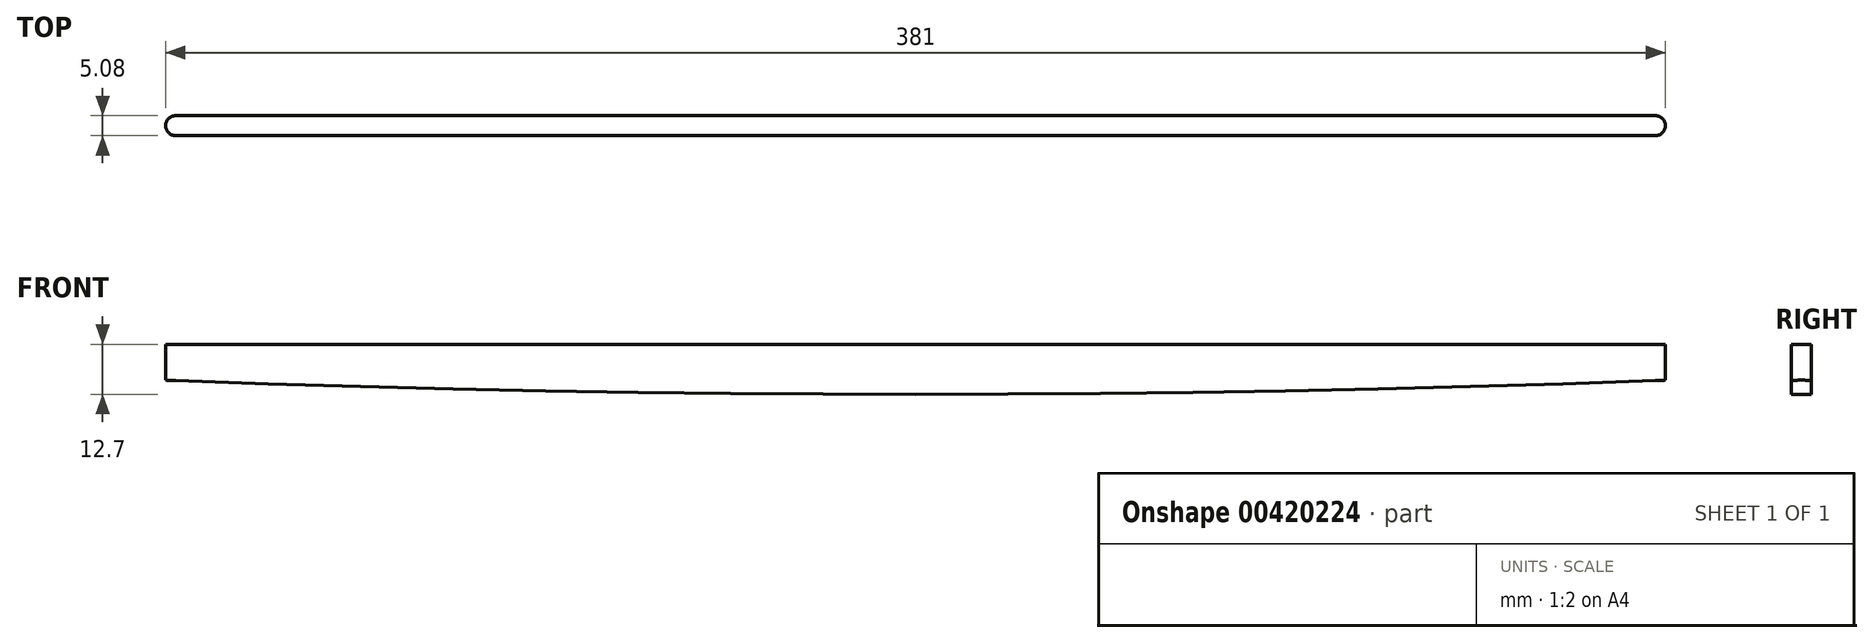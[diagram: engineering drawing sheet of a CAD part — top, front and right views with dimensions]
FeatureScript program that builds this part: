
annotation { "Feature Type Name" : "Feature", "Feature Type Description" : "" }
export const myFeature = defineFeature(function(context is Context, id is Id, definition is map)
    precondition{}
    {
        {
            var Q0;
            Q0=qCreatedBy(makeId("Front.planeOp"),FACE);
            var sketch = newSketch(context, id + "F0", { "sketchPlane" : qUnion([Q0])});
            skLineSegment(sketch, "E0", {"start": v(-319.44, 0) * mm, "end": v(61.56, 0) * mm});
            skArc(sketch, "E1", {"start": v(-319.44, -9.13) * mm, "mid": v(-128.94, -12.7) * mm, "end": v(61.56, -9.13) * mm});
            skPoint(sketch, "E2", {"position": v(-128.94, 0) * mm});
            skLineSegment(sketch, "E3", {"start": v(-128.94, 0) * mm, "end": v(-128.94, -12.7) * mm});
            skLineSegment(sketch, "E4", {"start": v(61.56, -9.13) * mm, "end": v(61.56, 0) * mm});
            skLineSegment(sketch, "E5", {"start": v(-319.44, 0) * mm, "end": v(-319.44, -9.13) * mm});
            skSolve(sketch);
        }
        {
            var Q0;
            Q0 = qSketchRegion(id + "F0", true);
            extrude(context, id + "F1", {"entities" : qUnion([Q0]), "endBound" : BoundingType.SYMMETRIC, "depth" : 5.08 * mm});
        }
        {
            var Q0;
            Q0=makeQuery(id+"F1.opExtrude","CAP_EDGE",EDGE,{"disambiguationData":[OSD([sQuery(id+"F0.wireOp",EDGE,"E5")])],"isStart":false});
            var Q1;
            Q1=makeQuery(id+"F1.opExtrude","CAP_EDGE",EDGE,{"disambiguationData":[OSD([sQuery(id+"F0.wireOp",EDGE,"E5")])],"isStart":true});
            var Q2;
            Q2=makeQuery(id+"F1.opExtrude","CAP_EDGE",EDGE,{"disambiguationData":[OSD([sQuery(id+"F0.wireOp",EDGE,"E4")])],"isStart":false});
            var Q3;
            Q3=makeQuery(id+"F1.opExtrude","CAP_EDGE",EDGE,{"disambiguationData":[OSD([sQuery(id+"F0.wireOp",EDGE,"E4")])],"isStart":true});
            fillet(context, id + "F2", {"entities" : qUnion([Q0, Q1, Q2, Q3]), "radius" : 2.54 * mm, "tangentPropagation" : true, "allowEdgeOverflow" : false});
        }
    });
